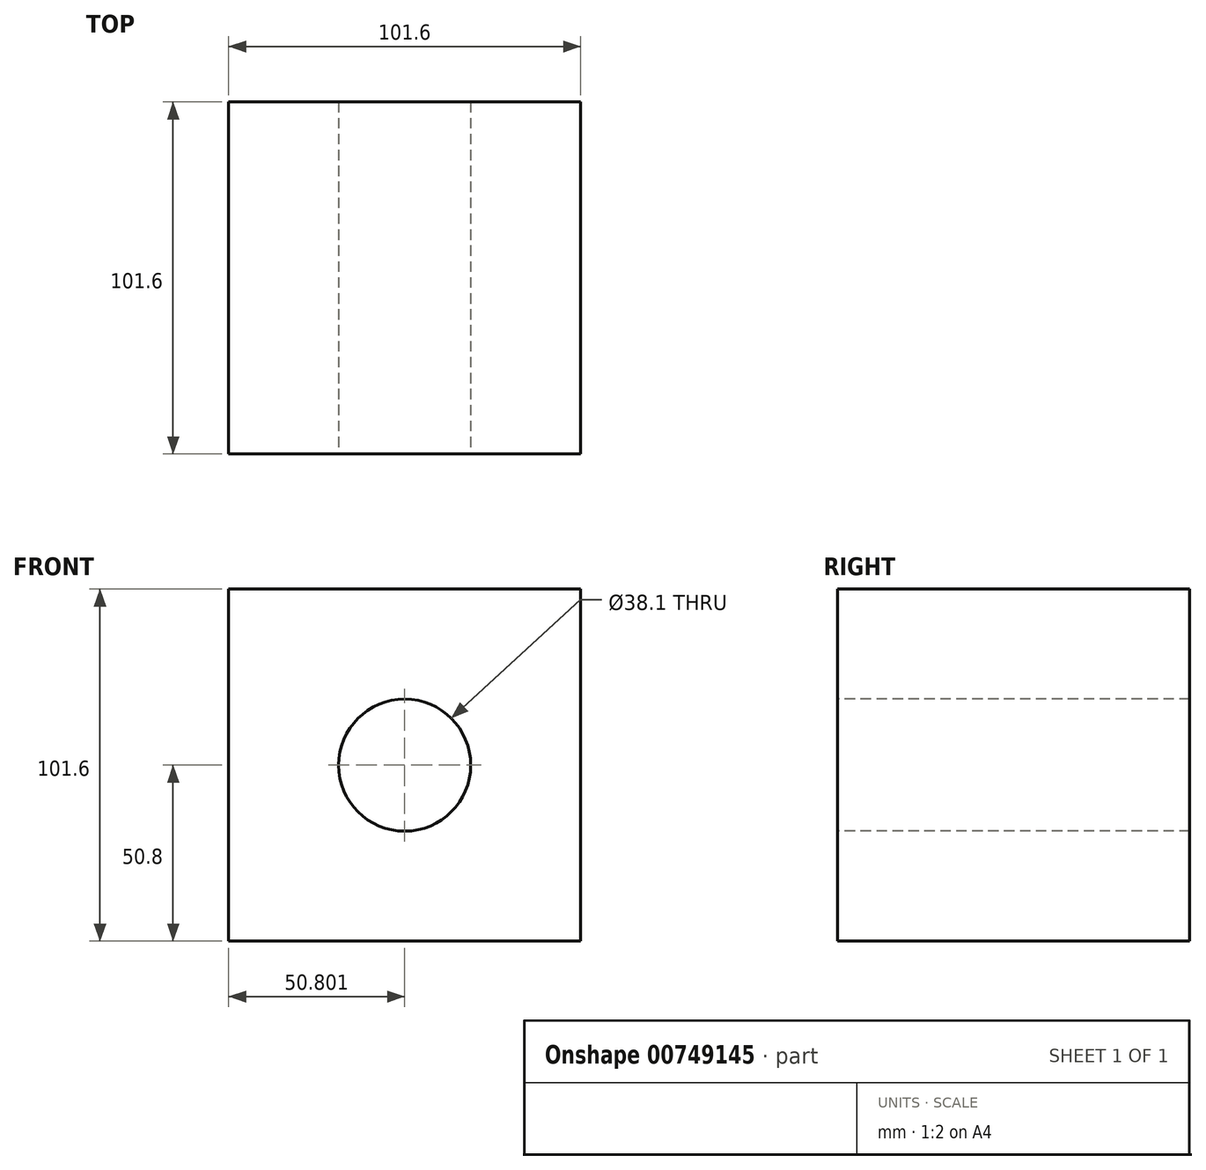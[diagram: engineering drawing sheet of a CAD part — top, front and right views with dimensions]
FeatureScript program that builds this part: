
annotation { "Feature Type Name" : "Feature", "Feature Type Description" : "" }
export const myFeature = defineFeature(function(context is Context, id is Id, definition is map)
    precondition{}
    {
        {
            var Q0;
            Q0=qCreatedBy(makeId("Top.planeOp"),FACE);
            var sketch = newSketch(context, id + "F0", { "sketchPlane" : qUnion([Q0])});
            skLineSegment(sketch, "E0.bottom", {"start": v(-41.38, 38.63) * mm, "end": v(60.22, 38.63) * mm});
            skLineSegment(sketch, "E0.top", {"start": v(-41.38, -62.97) * mm, "end": v(60.22, -62.97) * mm});
            skLineSegment(sketch, "E0.left", {"start": v(-41.38, 38.63) * mm, "end": v(-41.38, -62.97) * mm});
            skLineSegment(sketch, "E0.right", {"start": v(60.22, 38.63) * mm, "end": v(60.22, -62.97) * mm});
            skSolve(sketch);
        }
        {
            var Q0;
            Q0 = qSketchRegion(id + "F0", true);
            extrude(context, id + "F1", {"entities" : qUnion([Q0]), "depth" : 101.6 * mm, "offsetDistance" : 25.4 * mm});
        }
        {
            var Q0;
            Q0=makeQuery(id+"F1.opExtrude","SWEPT_FACE",FACE,{"disambiguationData":[OSD([sQuery(id+"F0.wireOp",EDGE,"E0.top")])]});
            var sketch = newSketch(context, id + "F2", { "sketchPlane" : qUnion([Q0])});
            skCircle(sketch, "E1.cCircle", {"center": v(9.42, 50.8) * mm, "radius": 19.04 * mm, "construction": true});
            skLineSegment(sketch, "E1.0", {"start": v(1.54, 69.84) * mm, "end": v(17.3, 69.84) * mm});
            skLineSegment(sketch, "E1.1", {"start": v(17.3, 69.84) * mm, "end": v(28.46, 58.68) * mm});
            skLineSegment(sketch, "E1.2", {"start": v(28.46, 58.68) * mm, "end": v(28.46, 42.92) * mm});
            skLineSegment(sketch, "E1.3", {"start": v(28.46, 42.92) * mm, "end": v(17.3, 31.76) * mm});
            skLineSegment(sketch, "E1.4", {"start": v(17.3, 31.76) * mm, "end": v(1.54, 31.76) * mm});
            skLineSegment(sketch, "E1.5", {"start": v(1.54, 31.76) * mm, "end": v(-9.61, 42.92) * mm});
            skLineSegment(sketch, "E1.6", {"start": v(-9.61, 42.92) * mm, "end": v(-9.61, 58.68) * mm});
            skLineSegment(sketch, "E1.7", {"start": v(-9.61, 58.68) * mm, "end": v(1.54, 69.84) * mm});
            skPoint(sketch, "E1.0.midPoint", {"position": v(9.42, 69.84) * mm});
            skPoint(sketch, "E2.orphan", {"position": v(-41.38, 50.8) * mm});
            skLineSegment(sketch, "E3.trimOffspring", {"start": v(9.42, 31.76) * mm, "end": v(9.42, 0) * mm, "construction": true});
            skPoint(sketch, "E4.end.orphan", {"position": v(60.22, 50.8) * mm});
            skPoint(sketch, "E5.orphan", {"position": v(9.42, 101.6) * mm});
            skCircle(sketch, "E6", {"center": v(9.42, 24.44) * mm, "radius": 2.17 * mm});
            skSolve(sketch);
        }
        {
            var Q0;
            Q0=sQuery(id+"F2.wireOp",VERTEX,"E1.cCircle.center");
            var Q1;
            Q1=makeQuery(id+"F1.opExtrude","SWEPT_BODY",BODY,{"disambiguationData":[OSD([sQuery(id+"F0.wireOp",EDGE,"E0.bottom"),sQuery(id+"F0.wireOp",EDGE,"E0.top"),sQuery(id+"F0.wireOp",EDGE,"E0.left"),sQuery(id+"F0.wireOp",EDGE,"E0.right")])]});
            hole(context, id + "F3", {"style" : HoleStyle.SIMPLE, "endStyle" : HoleEndStyle.THROUGH, "holeDiameter" : 38.1 * mm, "majorDiameter" : 6.35 * mm, "isTappedThrough" : true, "tappedDepth" : 12.7 * mm, "tapClearance" : 3, "locations" : qUnion([Q0]), "scope" : qUnion([Q1])});
        }
    });
